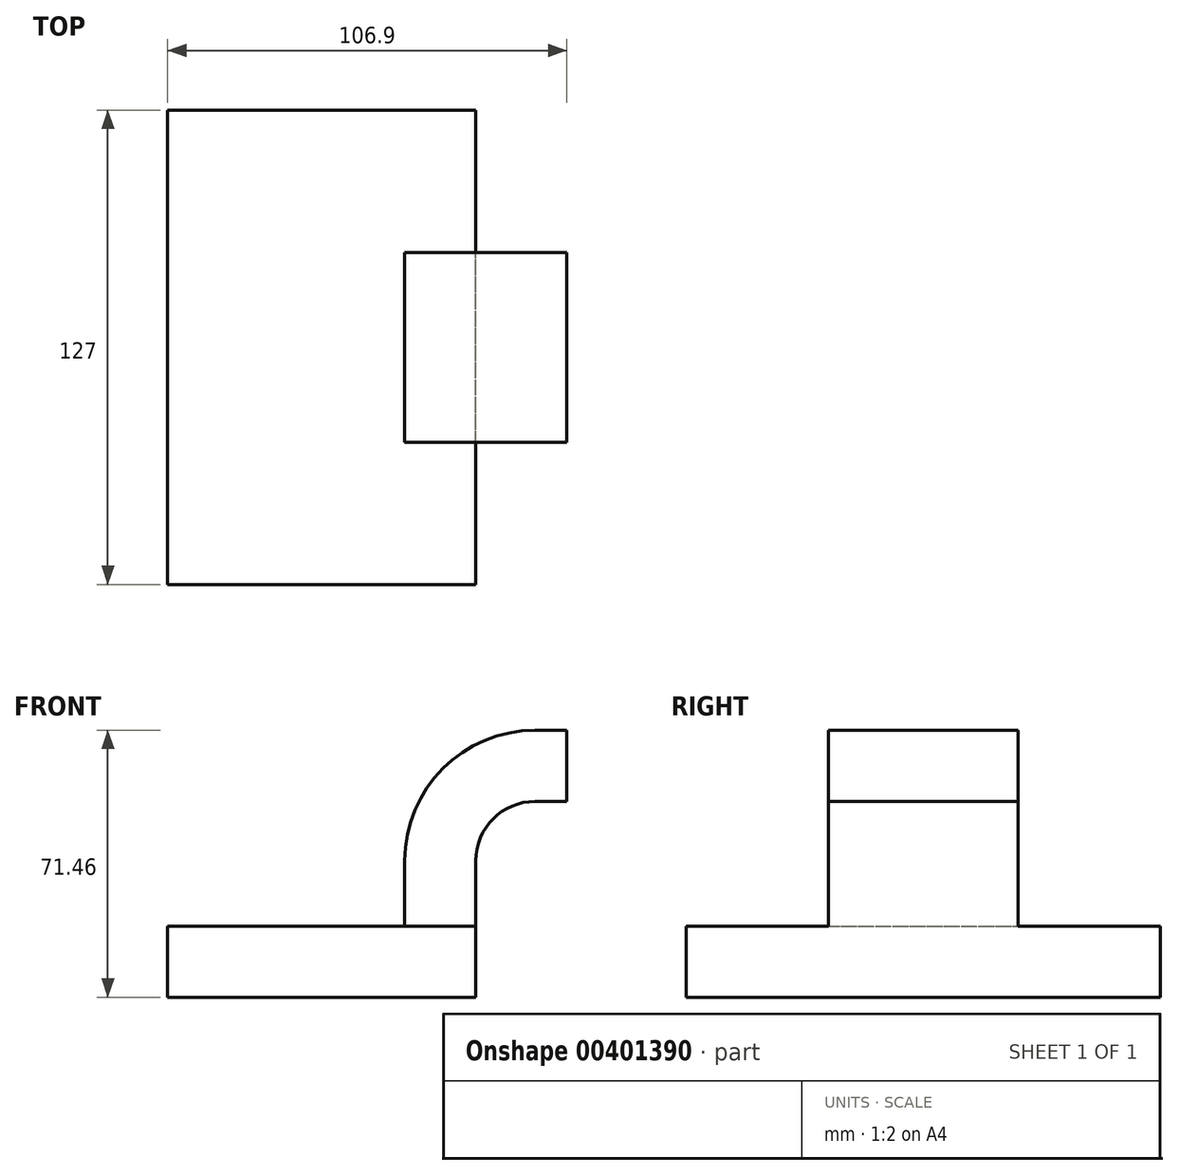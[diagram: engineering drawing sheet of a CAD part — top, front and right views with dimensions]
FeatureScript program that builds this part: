
annotation { "Feature Type Name" : "Feature", "Feature Type Description" : "" }
export const myFeature = defineFeature(function(context is Context, id is Id, definition is map)
    precondition{}
    {
        {
            var Q0;
            Q0=qCreatedBy(makeId("Front.planeOp"),FACE);
            var sketch = newSketch(context, id + "F0", { "sketchPlane" : qUnion([Q0])});
            skLineSegment(sketch, "E0.bottom", {"start": v(-41.28, 9.53) * mm, "end": v(41.28, 9.53) * mm});
            skLineSegment(sketch, "E0.top", {"start": v(-41.28, -9.53) * mm, "end": v(41.28, -9.53) * mm});
            skLineSegment(sketch, "E0.left", {"start": v(-41.28, 9.53) * mm, "end": v(-41.28, -9.53) * mm});
            skLineSegment(sketch, "E0.right", {"start": v(41.28, 9.53) * mm, "end": v(41.28, -9.53) * mm});
            skPoint(sketch, "E0.middle", {"position": v(0, 0) * mm});
            skLineSegment(sketch, "E1.bottom", {"start": v(65.63, 66.68) * mm, "end": v(116.43, 66.68) * mm});
            skLineSegment(sketch, "E1.top", {"start": v(65.63, 38.1) * mm, "end": v(116.43, 38.1) * mm});
            skLineSegment(sketch, "E1.left", {"start": v(65.63, 66.68) * mm, "end": v(65.63, 38.1) * mm});
            skLineSegment(sketch, "E1.right", {"start": v(116.43, 66.68) * mm, "end": v(116.43, 38.1) * mm});
            skLineSegment(sketch, "E2", {"start": v(41.27, 9.53) * mm, "end": v(41.27, 27) * mm});
            skArc(sketch, "E3", {"start": v(41.28, 27) * mm, "mid": v(45.92, 38.23) * mm, "end": v(57.15, 42.88) * mm});
            skLineSegment(sketch, "E4", {"start": v(57.15, 42.88) * mm, "end": v(97.73, 42.88) * mm});
            skLineSegment(sketch, "E5.0", {"start": v(57.15, 61.93) * mm, "end": v(97.73, 61.93) * mm});
            skArc(sketch, "E5.1", {"start": v(22.23, 27) * mm, "mid": v(32.45, 51.7) * mm, "end": v(57.15, 61.93) * mm});
            skLineSegment(sketch, "E5.2", {"start": v(22.23, 9.53) * mm, "end": v(22.23, 27) * mm});
            skLineSegment(sketch, "E6", {"start": v(97.18, 38.1) * mm, "end": v(97.73, 66.68) * mm});
            skFitSpline(sketch, "E7", {"points": [v(-41.28, 9.53) * mm, v(65.63, 61.93) * mm], "startDerivative": vector(29.4, 109.53) * mm, "endDerivative": vector(70.6, -13.7) * mm});
            skSolve(sketch);
        }
        {
            var Q0;
            Q0=makeQuery(id+"F0.imprint","IMPRINT",FACE,{"disambiguationData":[TD([[makeQuery(id+"F0.imprint","IMPRINT",EDGE,{"derivedFrom":sQuery(id+"F0.wireOp",EDGE,"E0.top")}),1.0]])]});
            extrude(context, id + "F1", {"entities" : qUnion([Q0]), "endBound" : BoundingType.SYMMETRIC, "depth" : 127 * mm});
        }
        {
            var Q0;
            {var subQ1=sQuery(id+"F0.wireOp",EDGE,"E2");Q0=makeQuery(id+"F0.imprint","IMPRINT",FACE,{"disambiguationData":[TD([[makeQuery(id+"F0.imprint","IMPRINT",EDGE,{"derivedFrom":subQ1}),1.0]])]});}
            extrude(context, id + "F2", {"entities" : qUnion([Q0]), "operationType" : NewBodyOperationType.ADD, "endBound" : BoundingType.SYMMETRIC, "depth" : 50.8 * mm});
        }
        {
            var Q0;
            {var subQ0=sQuery(id+"F0.wireOp",EDGE,"E5.1");Q0=makeQuery(id+"F0.imprint","IMPRINT",FACE,{"disambiguationData":[TD([[makeQuery(id+"F0.imprint","IMPRINT",EDGE,{"derivedFrom":subQ0}),1.0]])]});}
            extrude(context, id + "F3", {"entities" : qUnion([Q0]), "operationType" : NewBodyOperationType.ADD, "endBound" : BoundingType.SYMMETRIC, "depth" : 16.5 * mm});
        }
    });
